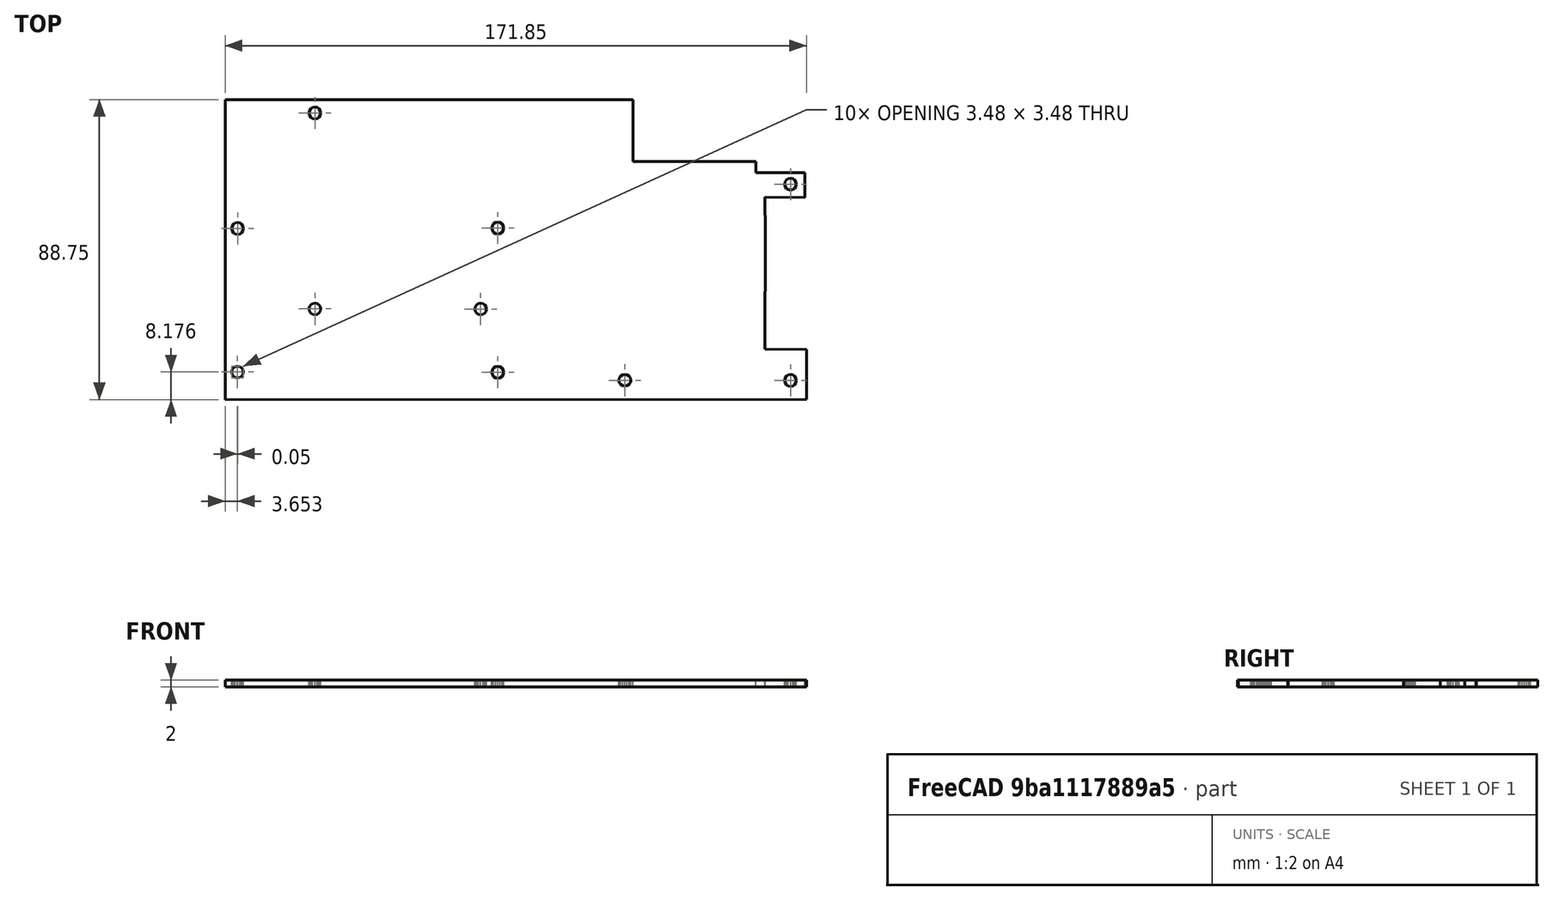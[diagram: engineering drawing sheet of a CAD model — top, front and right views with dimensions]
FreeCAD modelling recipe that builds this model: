
FCSTD DOCUMENT  (FreeCAD 0.19R24415 (Git))
Label: test_1
License: All rights reserved
LicenseURL: http://en.wikipedia.org/wiki/All_rights_reserved
objects: Sketcher::SketchObject×1, PartDesign::Pad×1, PartDesign::Body×1
note: 4 computed .brp shape members not serialized (recipe doc carries the construction recipe); baked Part::Feature solids carry a one-line shape summary decoded from their .brp

FEATURE [Sketcher::SketchObject] Sketch
  FullyConstrained = false
  MapMode = 5
  Support = -> [XY_Plane]
  sketch-geometry (174):
    g0: LineSegment StartX=77.4245 StartY=27.1042 StartZ=0 EndX=77.2919 EndY=26.4378 EndZ=0
    g1: LineSegment StartX=77.2919 StartY=26.4378 StartZ=0 EndX=76.9145 EndY=25.8728 EndZ=0
    g2: LineSegment StartX=76.9145 StartY=25.8728 StartZ=0 EndX=76.3495 EndY=25.4953 EndZ=0
    g3: LineSegment StartX=76.3495 StartY=25.4953 StartZ=0 EndX=75.6831 EndY=25.3628 EndZ=0
    g4: LineSegment StartX=75.6831 StartY=25.3628 StartZ=0 EndX=75.0167 EndY=25.4953 EndZ=0
    g5: LineSegment StartX=75.0167 StartY=25.4953 StartZ=0 EndX=74.4517 EndY=25.8728 EndZ=0
    g6: LineSegment StartX=74.4517 StartY=25.8728 StartZ=0 EndX=74.0742 EndY=26.4378 EndZ=0
    g7: LineSegment StartX=74.0742 StartY=26.4378 StartZ=0 EndX=73.9417 EndY=27.1042 EndZ=0
    g8: LineSegment StartX=73.9417 StartY=27.1042 StartZ=0 EndX=74.0785 EndY=27.782 EndZ=0
    g9: LineSegment StartX=74.0785 StartY=27.782 StartZ=0 EndX=74.4517 EndY=28.3356 EndZ=0
    g10: LineSegment StartX=74.4517 StartY=28.3356 StartZ=0 EndX=75.0053 EndY=28.7088 EndZ=0
    g11: LineSegment StartX=75.0053 StartY=28.7088 StartZ=0 EndX=75.6831 EndY=28.8456 EndZ=0
    g12: LineSegment StartX=75.6831 StartY=28.8456 StartZ=0 EndX=76.3495 EndY=28.7131 EndZ=0
    g13: LineSegment StartX=76.3495 StartY=28.7131 StartZ=0 EndX=76.9145 EndY=28.3356 EndZ=0
    g14: LineSegment StartX=76.9145 StartY=28.3356 StartZ=0 EndX=77.2919 EndY=27.7706 EndZ=0
    g15: LineSegment StartX=77.2919 StartY=27.7706 StartZ=0 EndX=77.4245 EndY=27.1042 EndZ=0
    g16: LineSegment StartX=157.033 StartY=67.5042 StartZ=0 EndX=171.483 EndY=67.5042 EndZ=0
    g17: LineSegment StartX=171.983 StartY=0.454206 StartZ=0 EndX=171.883 EndY=0.404206 EndZ=0
    g18: LineSegment StartX=171.883 StartY=0.404206 StartZ=0 EndX=0.133118 EndY=0.321209 EndZ=0
    g19: LineSegment StartX=171.533 StartY=60.1542 StartZ=0 EndX=159.683 EndY=60.2542 EndZ=0
    g20: LineSegment StartX=159.683 StartY=60.2542 StartZ=0 EndX=159.783 EndY=49.4542 EndZ=0
    g21: LineSegment StartX=82.4745 StartY=8.40421 StartZ=0 EndX=82.3419 EndY=7.7378 EndZ=0
    g22: LineSegment StartX=82.3419 StartY=7.7378 StartZ=0 EndX=81.9645 EndY=7.17285 EndZ=0
    g23: LineSegment StartX=81.9645 StartY=7.17285 StartZ=0 EndX=81.3995 EndY=6.79536 EndZ=0
    g24: LineSegment StartX=81.3995 StartY=6.79536 StartZ=0 EndX=80.7331 EndY=6.6628 EndZ=0
    g25: LineSegment StartX=80.7331 StartY=6.6628 StartZ=0 EndX=80.0667 EndY=6.79536 EndZ=0
    g26: LineSegment StartX=80.0667 StartY=6.79536 StartZ=0 EndX=79.5017 EndY=7.17285 EndZ=0
    g27: LineSegment StartX=79.5017 StartY=7.17285 StartZ=0 EndX=79.1242 EndY=7.7378 EndZ=0
    g28: LineSegment StartX=79.1242 StartY=7.7378 StartZ=0 EndX=78.9917 EndY=8.40421 EndZ=0
    g29: LineSegment StartX=78.9917 StartY=8.40421 StartZ=0 EndX=79.1242 EndY=9.07062 EndZ=0
    g30: LineSegment StartX=79.1242 StartY=9.07062 StartZ=0 EndX=79.5017 EndY=9.63557 EndZ=0
    g31: LineSegment StartX=79.5017 StartY=9.63557 StartZ=0 EndX=80.0667 EndY=10.0131 EndZ=0
    g32: LineSegment StartX=80.0667 StartY=10.0131 StartZ=0 EndX=80.7331 EndY=10.1456 EndZ=0
    g33: LineSegment StartX=80.7331 StartY=10.1456 StartZ=0 EndX=81.3995 EndY=10.0131 EndZ=0
    g34: LineSegment StartX=81.3995 StartY=10.0131 StartZ=0 EndX=81.9645 EndY=9.63557 EndZ=0
    g35: LineSegment StartX=81.9645 StartY=9.63557 StartZ=0 EndX=82.3419 EndY=9.07062 EndZ=0
    g36: LineSegment StartX=82.3419 StartY=9.07062 StartZ=0 EndX=82.4745 EndY=8.40421 EndZ=0
    g37: LineSegment StartX=120.783 StartY=70.8212 StartZ=0 EndX=157.033 EndY=70.7542 EndZ=0
    g38: LineSegment StartX=28.4245 StartY=27.1542 StartZ=0 EndX=28.2919 EndY=26.4878 EndZ=0
    g39: LineSegment StartX=28.2919 StartY=26.4878 StartZ=0 EndX=27.9145 EndY=25.9228 EndZ=0
    g40: LineSegment StartX=27.9145 StartY=25.9228 StartZ=0 EndX=27.3495 EndY=25.5453 EndZ=0
    g41: LineSegment StartX=27.3495 StartY=25.5453 StartZ=0 EndX=26.6831 EndY=25.4128 EndZ=0
    g42: LineSegment StartX=26.6831 StartY=25.4128 StartZ=0 EndX=26.0053 EndY=25.5496 EndZ=0
    g43: LineSegment StartX=26.0053 StartY=25.5496 StartZ=0 EndX=25.4517 EndY=25.9228 EndZ=0
    g44: LineSegment StartX=25.4517 StartY=25.9228 StartZ=0 EndX=25.0785 EndY=26.4764 EndZ=0
    g45: LineSegment StartX=25.0785 StartY=26.4764 StartZ=0 EndX=24.9417 EndY=27.1542 EndZ=0
    g46: LineSegment StartX=24.9417 StartY=27.1542 StartZ=0 EndX=25.0785 EndY=27.832 EndZ=0
    g47: LineSegment StartX=25.0785 StartY=27.832 StartZ=0 EndX=25.4517 EndY=28.3856 EndZ=0
    g48: LineSegment StartX=25.4517 StartY=28.3856 StartZ=0 EndX=26.0053 EndY=28.7588 EndZ=0
    g49: LineSegment StartX=26.0053 StartY=28.7588 StartZ=0 EndX=26.6831 EndY=28.8956 EndZ=0
    g50: LineSegment StartX=26.6831 StartY=28.8956 StartZ=0 EndX=27.3495 EndY=28.7631 EndZ=0
    g51: LineSegment StartX=27.3495 StartY=28.7631 StartZ=0 EndX=27.9145 EndY=28.3856 EndZ=0
    g52: LineSegment StartX=27.9145 StartY=28.3856 StartZ=0 EndX=28.2919 EndY=27.8206 EndZ=0
    g53: LineSegment StartX=28.2919 StartY=27.8206 StartZ=0 EndX=28.4245 EndY=27.1542 EndZ=0
    g54: LineSegment StartX=120.025 StartY=6.05421 StartZ=0 EndX=119.892 EndY=5.3878 EndZ=0
    g55: LineSegment StartX=119.892 StartY=5.3878 StartZ=0 EndX=119.515 EndY=4.82285 EndZ=0
    g56: LineSegment StartX=119.515 StartY=4.82285 StartZ=0 EndX=118.95 EndY=4.44536 EndZ=0
    g57: LineSegment StartX=118.95 StartY=4.44536 StartZ=0 EndX=118.284 EndY=4.3128 EndZ=0
    g58: LineSegment StartX=118.284 StartY=4.3128 StartZ=0 EndX=117.617 EndY=4.44536 EndZ=0
    g59: LineSegment StartX=117.617 StartY=4.44536 StartZ=0 EndX=117.052 EndY=4.82285 EndZ=0
    g60: LineSegment StartX=117.052 StartY=4.82285 StartZ=0 EndX=116.675 EndY=5.3878 EndZ=0
    g61: LineSegment StartX=116.675 StartY=5.3878 StartZ=0 EndX=116.542 EndY=6.05421 EndZ=0
    g62: LineSegment StartX=116.542 StartY=6.05421 StartZ=0 EndX=116.675 EndY=6.72062 EndZ=0
    g63: LineSegment StartX=116.675 StartY=6.72062 StartZ=0 EndX=117.052 EndY=7.28557 EndZ=0
    g64: LineSegment StartX=117.052 StartY=7.28557 StartZ=0 EndX=117.617 EndY=7.66306 EndZ=0
    g65: LineSegment StartX=117.617 StartY=7.66306 StartZ=0 EndX=118.284 EndY=7.79562 EndZ=0
    g66: LineSegment StartX=118.284 StartY=7.79562 StartZ=0 EndX=118.95 EndY=7.66306 EndZ=0
    g67: LineSegment StartX=118.95 StartY=7.66306 StartZ=0 EndX=119.515 EndY=7.28557 EndZ=0
    g68: LineSegment StartX=119.515 StartY=7.28557 StartZ=0 EndX=119.892 EndY=6.72062 EndZ=0
    g69: LineSegment StartX=119.892 StartY=6.72062 StartZ=0 EndX=120.025 EndY=6.05421 EndZ=0
    g70: LineSegment StartX=169.033 StartY=6.00421 StartZ=0 EndX=168.9 EndY=5.3378 EndZ=0
    g71: LineSegment StartX=168.9 StartY=5.3378 StartZ=0 EndX=168.523 EndY=4.77285 EndZ=0
    g72: LineSegment StartX=168.523 StartY=4.77285 StartZ=0 EndX=167.958 EndY=4.39536 EndZ=0
    g73: LineSegment StartX=167.958 StartY=4.39536 StartZ=0 EndX=167.292 EndY=4.2628 EndZ=0
    g74: LineSegment StartX=167.292 StartY=4.2628 StartZ=0 EndX=166.614 EndY=4.39965 EndZ=0
    g75: LineSegment StartX=166.614 StartY=4.39965 StartZ=0 EndX=166.06 EndY=4.77285 EndZ=0
    g76: LineSegment StartX=166.06 StartY=4.77285 StartZ=0 EndX=165.687 EndY=5.32638 EndZ=0
    g77: LineSegment StartX=165.687 StartY=5.32638 StartZ=0 EndX=165.55 EndY=6.00421 EndZ=0
    g78: LineSegment StartX=165.55 StartY=6.00421 StartZ=0 EndX=165.687 EndY=6.68204 EndZ=0
    g79: LineSegment StartX=165.687 StartY=6.68204 StartZ=0 EndX=166.06 EndY=7.23557 EndZ=0
    g80: LineSegment StartX=166.06 StartY=7.23557 StartZ=0 EndX=166.614 EndY=7.60877 EndZ=0
    g81: LineSegment StartX=166.614 StartY=7.60877 StartZ=0 EndX=167.292 EndY=7.74562 EndZ=0
    g82: LineSegment StartX=167.292 StartY=7.74562 StartZ=0 EndX=167.958 EndY=7.61306 EndZ=0
    g83: LineSegment StartX=167.958 StartY=7.61306 StartZ=0 EndX=168.523 EndY=7.23557 EndZ=0
    g84: LineSegment StartX=168.523 StartY=7.23557 StartZ=0 EndX=168.9 EndY=6.67062 EndZ=0
    g85: LineSegment StartX=168.9 StartY=6.67062 StartZ=0 EndX=169.033 EndY=6.00421 EndZ=0
    g86: LineSegment StartX=159.683 StartY=15.2042 StartZ=0 EndX=171.983 EndY=15.1542 EndZ=0
    g87: LineSegment StartX=82.4745 StartY=51.0956 StartZ=0 EndX=82.3419 EndY=50.4292 EndZ=0
    g88: LineSegment StartX=82.3419 StartY=50.4292 StartZ=0 EndX=81.9645 EndY=49.8642 EndZ=0
    g89: LineSegment StartX=81.9645 StartY=49.8642 StartZ=0 EndX=81.3995 EndY=49.4867 EndZ=0
    g90: LineSegment StartX=81.3995 StartY=49.4867 StartZ=0 EndX=80.7331 EndY=49.3542 EndZ=0
    g91: LineSegment StartX=80.7331 StartY=49.3542 StartZ=0 EndX=80.0667 EndY=49.4867 EndZ=0
    g92: LineSegment StartX=80.0667 StartY=49.4867 StartZ=0 EndX=79.5017 EndY=49.8642 EndZ=0
    g93: LineSegment StartX=79.5017 StartY=49.8642 StartZ=0 EndX=79.1242 EndY=50.4292 EndZ=0
    g94: LineSegment StartX=79.1242 StartY=50.4292 StartZ=0 EndX=78.9917 EndY=51.0956 EndZ=0
    g95: LineSegment StartX=78.9917 StartY=51.0956 StartZ=0 EndX=79.1242 EndY=51.762 EndZ=0
    g96: LineSegment StartX=79.1242 StartY=51.762 StartZ=0 EndX=79.5017 EndY=52.327 EndZ=0
    g97: LineSegment StartX=79.5017 StartY=52.327 StartZ=0 EndX=80.0667 EndY=52.7045 EndZ=0
    g98: LineSegment StartX=80.0667 StartY=52.7045 StartZ=0 EndX=80.7331 EndY=52.837 EndZ=0
    g99: LineSegment StartX=80.7331 StartY=52.837 StartZ=0 EndX=81.3995 EndY=52.7045 EndZ=0
    g100: LineSegment StartX=81.3995 StartY=52.7045 StartZ=0 EndX=81.9645 EndY=52.327 EndZ=0
    g101: LineSegment StartX=81.9645 StartY=52.327 StartZ=0 EndX=82.3419 EndY=51.762 EndZ=0
    g102: LineSegment StartX=82.3419 StartY=51.762 StartZ=0 EndX=82.4745 EndY=51.0956 EndZ=0
    g103: LineSegment StartX=0.133118 StartY=0.321209 StartZ=0 EndX=0.133118 EndY=89.0212 EndZ=0
    g104: LineSegment StartX=169.033 StartY=64.0542 StartZ=0 EndX=168.9 EndY=63.3878 EndZ=0
    g105: LineSegment StartX=168.9 StartY=63.3878 StartZ=0 EndX=168.523 EndY=62.8228 EndZ=0
    g106: LineSegment StartX=168.523 StartY=62.8228 StartZ=0 EndX=167.958 EndY=62.4453 EndZ=0
    g107: LineSegment StartX=167.958 StartY=62.4453 StartZ=0 EndX=167.292 EndY=62.3128 EndZ=0
    g108: LineSegment StartX=167.292 StartY=62.3128 StartZ=0 EndX=166.614 EndY=62.4496 EndZ=0
    g109: LineSegment StartX=166.614 StartY=62.4496 StartZ=0 EndX=166.06 EndY=62.8228 EndZ=0
    g110: LineSegment StartX=166.06 StartY=62.8228 StartZ=0 EndX=165.687 EndY=63.3764 EndZ=0
    g111: LineSegment StartX=165.687 StartY=63.3764 StartZ=0 EndX=165.55 EndY=64.0542 EndZ=0
    g112: LineSegment StartX=165.55 StartY=64.0542 StartZ=0 EndX=165.687 EndY=64.732 EndZ=0
    g113: LineSegment StartX=165.687 StartY=64.732 StartZ=0 EndX=166.06 EndY=65.2856 EndZ=0
    g114: LineSegment StartX=166.06 StartY=65.2856 StartZ=0 EndX=166.614 EndY=65.6588 EndZ=0
    g115: LineSegment StartX=166.614 StartY=65.6588 StartZ=0 EndX=167.292 EndY=65.7956 EndZ=0
    g116: LineSegment StartX=167.292 StartY=65.7956 StartZ=0 EndX=167.958 EndY=65.6631 EndZ=0
    g117: LineSegment StartX=167.958 StartY=65.6631 StartZ=0 EndX=168.523 EndY=65.2856 EndZ=0
    g118: LineSegment StartX=168.523 StartY=65.2856 StartZ=0 EndX=168.9 EndY=64.7206 EndZ=0
    g119: LineSegment StartX=168.9 StartY=64.7206 StartZ=0 EndX=169.033 EndY=64.0542 EndZ=0
    g120: LineSegment StartX=28.4245 StartY=85.1042 StartZ=0 EndX=28.2876 EndY=84.4264 EndZ=0
    g121: LineSegment StartX=28.2876 StartY=84.4264 StartZ=0 EndX=27.9145 EndY=83.8728 EndZ=0
    g122: LineSegment StartX=27.9145 StartY=83.8728 StartZ=0 EndX=27.3609 EndY=83.4997 EndZ=0
    g123: LineSegment StartX=27.3609 StartY=83.4997 StartZ=0 EndX=26.6831 EndY=83.3628 EndZ=0
    g124: LineSegment StartX=26.6831 StartY=83.3628 StartZ=0 EndX=26.0053 EndY=83.4997 EndZ=0
    g125: LineSegment StartX=26.0053 StartY=83.4997 StartZ=0 EndX=25.4517 EndY=83.8728 EndZ=0
    g126: LineSegment StartX=25.4517 StartY=83.8728 StartZ=0 EndX=25.0785 EndY=84.4264 EndZ=0
    g127: LineSegment StartX=25.0785 StartY=84.4264 StartZ=0 EndX=24.9417 EndY=85.1042 EndZ=0
    g128: LineSegment StartX=24.9417 StartY=85.1042 StartZ=0 EndX=25.0785 EndY=85.782 EndZ=0
    g129: LineSegment StartX=25.0785 StartY=85.782 StartZ=0 EndX=25.4517 EndY=86.3356 EndZ=0
    g130: LineSegment StartX=25.4517 StartY=86.3356 StartZ=0 EndX=26.0053 EndY=86.7087 EndZ=0
    g131: LineSegment StartX=26.0053 StartY=86.7087 StartZ=0 EndX=26.6831 EndY=86.8456 EndZ=0
    g132: LineSegment StartX=26.6831 StartY=86.8456 StartZ=0 EndX=27.3609 EndY=86.7087 EndZ=0
    g133: LineSegment StartX=27.3609 StartY=86.7087 StartZ=0 EndX=27.9145 EndY=86.3356 EndZ=0
    g134: LineSegment StartX=27.9145 StartY=86.3356 StartZ=0 EndX=28.2876 EndY=85.782 EndZ=0
    g135: LineSegment StartX=28.2876 StartY=85.782 StartZ=0 EndX=28.4245 EndY=85.1042 EndZ=0
    g136: LineSegment StartX=171.483 StartY=67.5042 StartZ=0 EndX=171.533 EndY=60.1542 EndZ=0
    g137: LineSegment StartX=159.783 StartY=49.4542 StartZ=0 EndX=159.683 EndY=15.2042 EndZ=0
    g138: LineSegment StartX=0.133118 StartY=89.0212 StartZ=0 EndX=120.783 EndY=89.0712 EndZ=0
    g139: LineSegment StartX=171.983 StartY=15.1542 StartZ=0 EndX=171.983 EndY=0.454206 EndZ=0
    g140: LineSegment StartX=5.57453 StartY=50.9456 StartZ=0 EndX=5.43768 EndY=50.2678 EndZ=0
    g141: LineSegment StartX=5.43768 StartY=50.2678 StartZ=0 EndX=5.06448 EndY=49.7142 EndZ=0
    g142: LineSegment StartX=5.06448 StartY=49.7142 StartZ=0 EndX=4.51095 EndY=49.341 EndZ=0
    g143: LineSegment StartX=4.51095 StartY=49.341 StartZ=0 EndX=3.83312 EndY=49.2042 EndZ=0
    g144: LineSegment StartX=3.83312 StartY=49.2042 StartZ=0 EndX=3.15529 EndY=49.341 EndZ=0
    g145: LineSegment StartX=3.15529 StartY=49.341 StartZ=0 EndX=2.60176 EndY=49.7142 EndZ=0
    g146: LineSegment StartX=2.60176 StartY=49.7142 StartZ=0 EndX=2.22856 EndY=50.2678 EndZ=0
    g147: LineSegment StartX=2.22856 StartY=50.2678 StartZ=0 EndX=2.09171 EndY=50.9456 EndZ=0
    g148: LineSegment StartX=2.09171 StartY=50.9456 StartZ=0 EndX=2.22856 EndY=51.6234 EndZ=0
    g149: LineSegment StartX=2.22856 StartY=51.6234 StartZ=0 EndX=2.60176 EndY=52.177 EndZ=0
    g150: LineSegment StartX=2.60176 StartY=52.177 StartZ=0 EndX=3.15529 EndY=52.5502 EndZ=0
    g151: LineSegment StartX=3.15529 StartY=52.5502 StartZ=0 EndX=3.83312 EndY=52.687 EndZ=0
    g152: LineSegment StartX=3.83312 StartY=52.687 StartZ=0 EndX=4.51095 EndY=52.5502 EndZ=0
    g153: LineSegment StartX=4.51095 StartY=52.5502 StartZ=0 EndX=5.06448 EndY=52.177 EndZ=0
    g154: LineSegment StartX=5.06448 StartY=52.177 StartZ=0 EndX=5.43768 EndY=51.6234 EndZ=0
    g155: LineSegment StartX=5.43768 StartY=51.6234 StartZ=0 EndX=5.57453 EndY=50.9456 EndZ=0
    g156: LineSegment StartX=120.783 StartY=89.0712 StartZ=0 EndX=120.783 EndY=70.8212 EndZ=0
    g157: LineSegment StartX=157.033 StartY=70.7542 StartZ=0 EndX=157.033 EndY=67.5042 EndZ=0
    g158: LineSegment StartX=5.52453 StartY=8.49562 StartZ=0 EndX=5.39197 EndY=7.82921 EndZ=0
    g159: LineSegment StartX=5.39197 StartY=7.82921 StartZ=0 EndX=5.01448 EndY=7.26426 EndZ=0
    g160: LineSegment StartX=5.01448 StartY=7.26426 StartZ=0 EndX=4.44953 EndY=6.88677 EndZ=0
    g161: LineSegment StartX=4.44953 StartY=6.88677 StartZ=0 EndX=3.78312 EndY=6.75421 EndZ=0
    g162: LineSegment StartX=3.78312 StartY=6.75421 StartZ=0 EndX=3.11671 EndY=6.88677 EndZ=0
    g163: LineSegment StartX=3.11671 StartY=6.88677 StartZ=0 EndX=2.55176 EndY=7.26426 EndZ=0
    g164: LineSegment StartX=2.55176 StartY=7.26426 StartZ=0 EndX=2.17427 EndY=7.82921 EndZ=0
    g165: LineSegment StartX=2.17427 StartY=7.82921 StartZ=0 EndX=2.04171 EndY=8.49562 EndZ=0
    g166: LineSegment StartX=2.04171 StartY=8.49562 StartZ=0 EndX=2.17857 EndY=9.17345 EndZ=0
    g167: LineSegment StartX=2.17857 StartY=9.17345 StartZ=0 EndX=2.55177 EndY=9.72696 EndZ=0
    g168: LineSegment StartX=2.55177 StartY=9.72696 StartZ=0 EndX=3.10529 EndY=10.1002 EndZ=0
    g169: LineSegment StartX=3.10529 StartY=10.1002 StartZ=0 EndX=3.78312 EndY=10.237 EndZ=0
    g170: LineSegment StartX=3.78312 StartY=10.237 StartZ=0 EndX=4.46095 EndY=10.1002 EndZ=0
    g171: LineSegment StartX=4.46095 StartY=10.1002 StartZ=0 EndX=5.01447 EndY=9.72696 EndZ=0
    g172: LineSegment StartX=5.01447 StartY=9.72696 StartZ=0 EndX=5.38767 EndY=9.17345 EndZ=0
    g173: LineSegment StartX=5.38767 StartY=9.17345 StartZ=0 EndX=5.52453 EndY=8.49562 EndZ=0
FEATURE [PartDesign::Pad] Pad
  Direction = (1,1,1)
  Length = 2
  Length2 = 100
  Profile = -> Sketch
  Type = 0
FEATURE [PartDesign::Body] Body
  Group = -> [Sketch,Pad]
  Origin = -> Origin
  Tip = -> Pad
